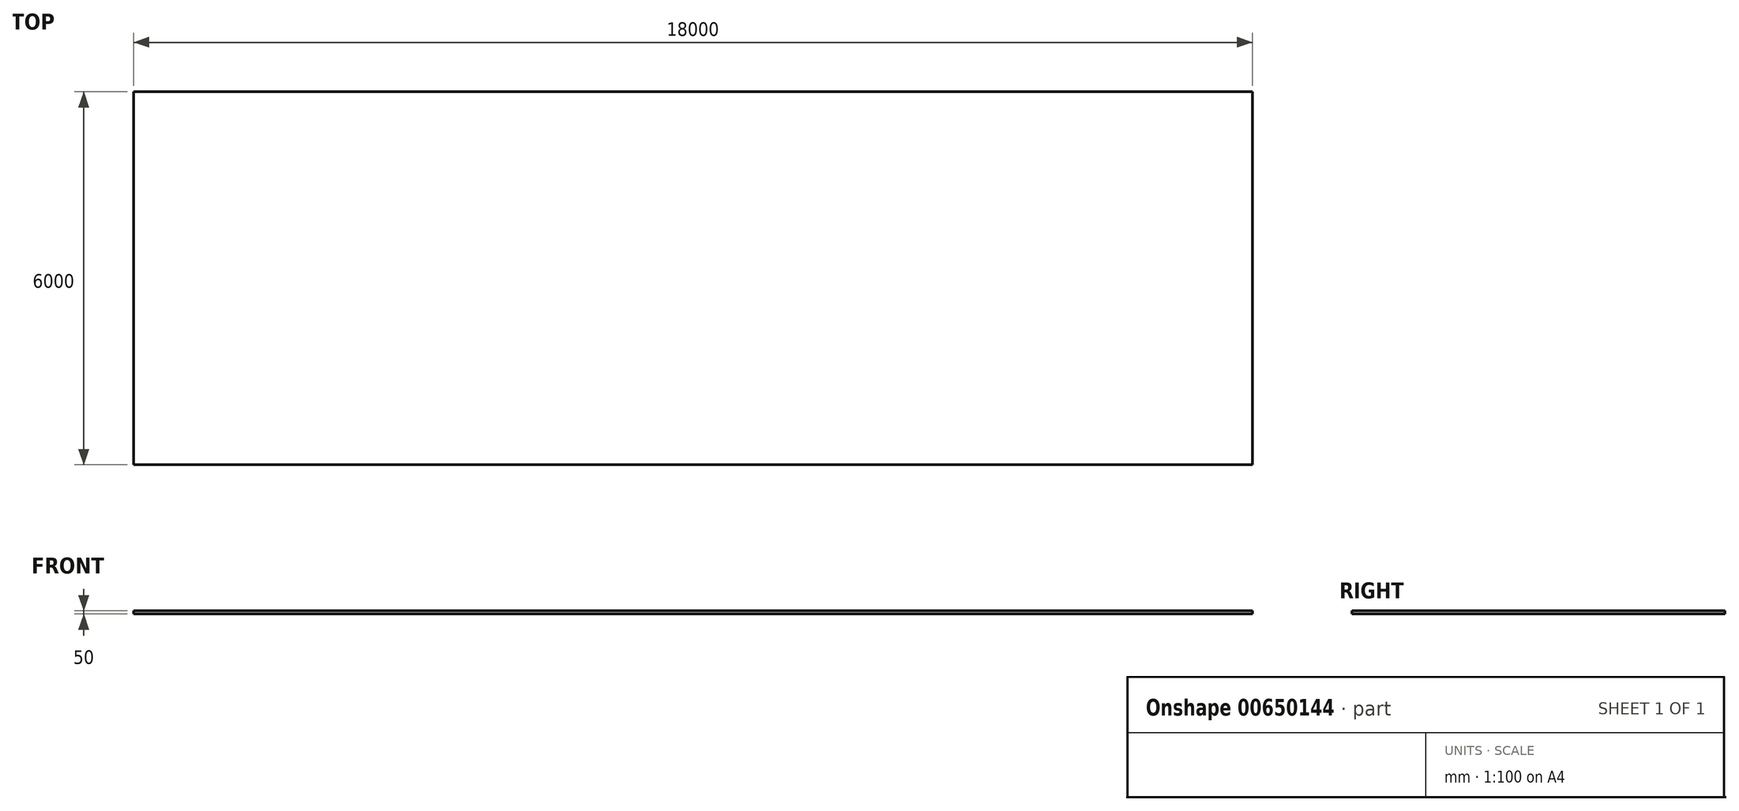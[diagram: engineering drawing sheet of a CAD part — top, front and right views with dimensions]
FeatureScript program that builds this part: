
annotation { "Feature Type Name" : "Feature", "Feature Type Description" : "" }
export const myFeature = defineFeature(function(context is Context, id is Id, definition is map)
    precondition{}
    {
        {
            var Q0;
            Q0=qCreatedBy(makeId("Top.planeOp"),FACE);
            var sketch = newSketch(context, id + "F0", { "sketchPlane" : qUnion([Q0])});
            skLineSegment(sketch, "E0.bottom", {"start": v(-9000, 3000) * mm, "end": v(9000, 3000) * mm});
            skLineSegment(sketch, "E0.top", {"start": v(-9000, -3000) * mm, "end": v(9000, -3000) * mm});
            skLineSegment(sketch, "E0.left", {"start": v(-9000, 3000) * mm, "end": v(-9000, -3000) * mm});
            skLineSegment(sketch, "E0.right", {"start": v(9000, 3000) * mm, "end": v(9000, -3000) * mm});
            skPoint(sketch, "E0.middle", {"position": v(0, 0) * mm});
            skSolve(sketch);
        }
        {
            var Q0;
            Q0 = qSketchRegion(id + "F0", true);
            extrude(context, id + "F1", {"entities" : qUnion([Q0]), "depth" : 50 * mm, "offsetDistance" : 25 * mm});
        }
    });
